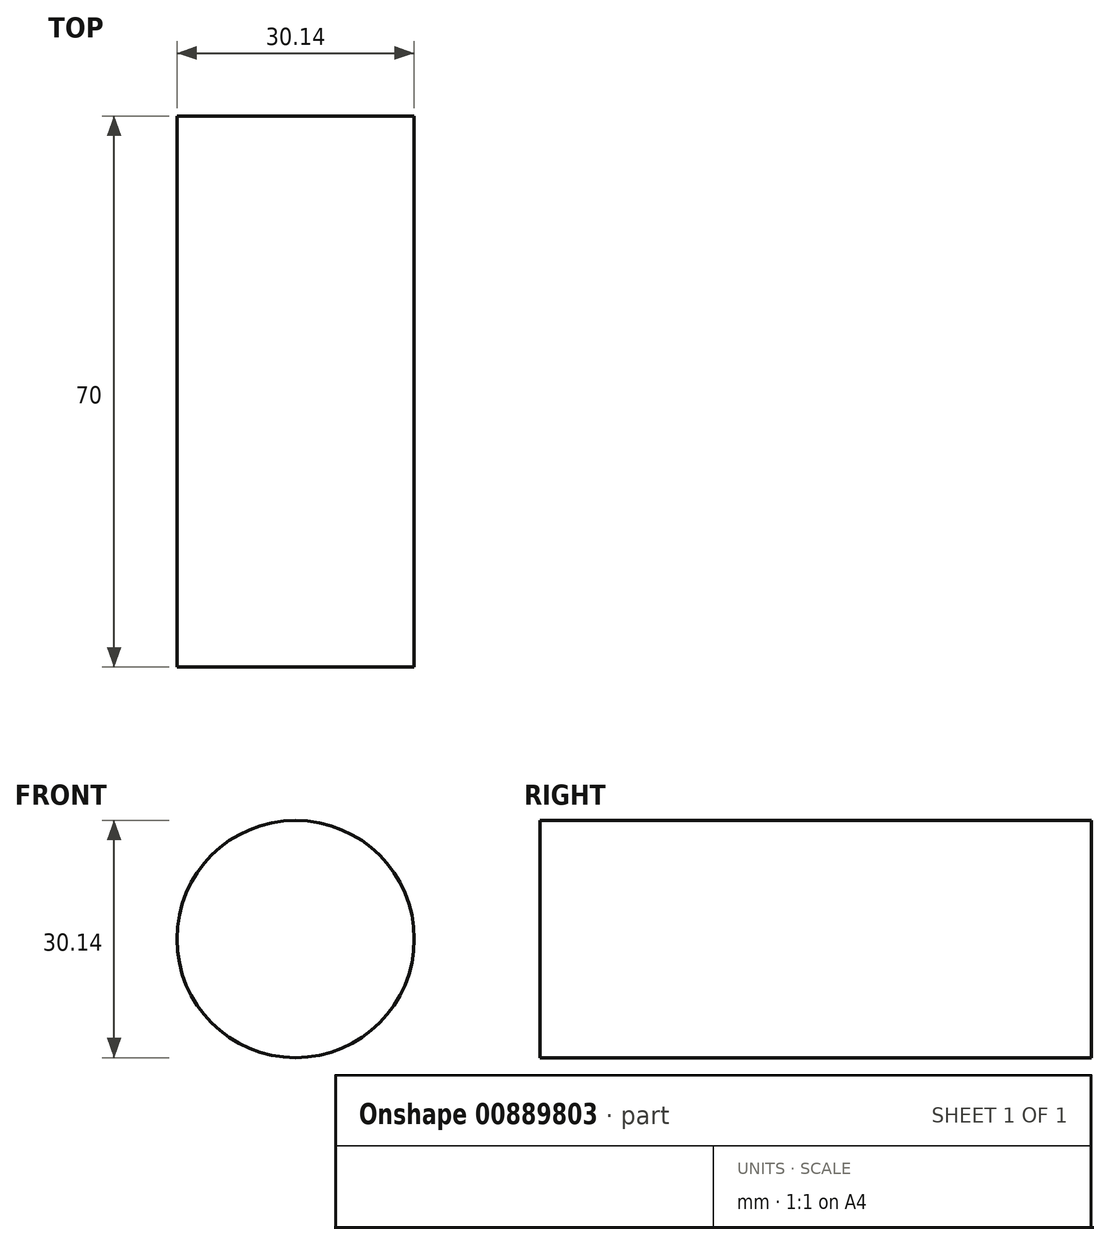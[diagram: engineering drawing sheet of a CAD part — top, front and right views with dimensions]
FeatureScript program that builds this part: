
annotation { "Feature Type Name" : "Feature", "Feature Type Description" : "" }
export const myFeature = defineFeature(function(context is Context, id is Id, definition is map)
    precondition{}
    {
        {
            var Q0;
            Q0=qCreatedBy(makeId("Front.planeOp"),FACE);
            var sketch = newSketch(context, id + "F0", { "sketchPlane" : qUnion([Q0])});
            skCircle(sketch, "E0", {"center": v(0, 0) * mm, "radius": 15.07 * mm});
            skSolve(sketch);
        }
        {
            var Q0;
            Q0=makeQuery(id+"F0.imprint","IMPRINT",FACE,{"disambiguationData":[TD([[makeQuery(id+"F0.imprint","IMPRINT",EDGE,{"derivedFrom":sQuery(id+"F0.wireOp",EDGE,"E0")}),1.0]])]});
            extrude(context, id + "F1", {"entities" : qUnion([Q0]), "depth" : 70 * mm, "offsetDistance" : 25.4 * mm});
        }
    });
